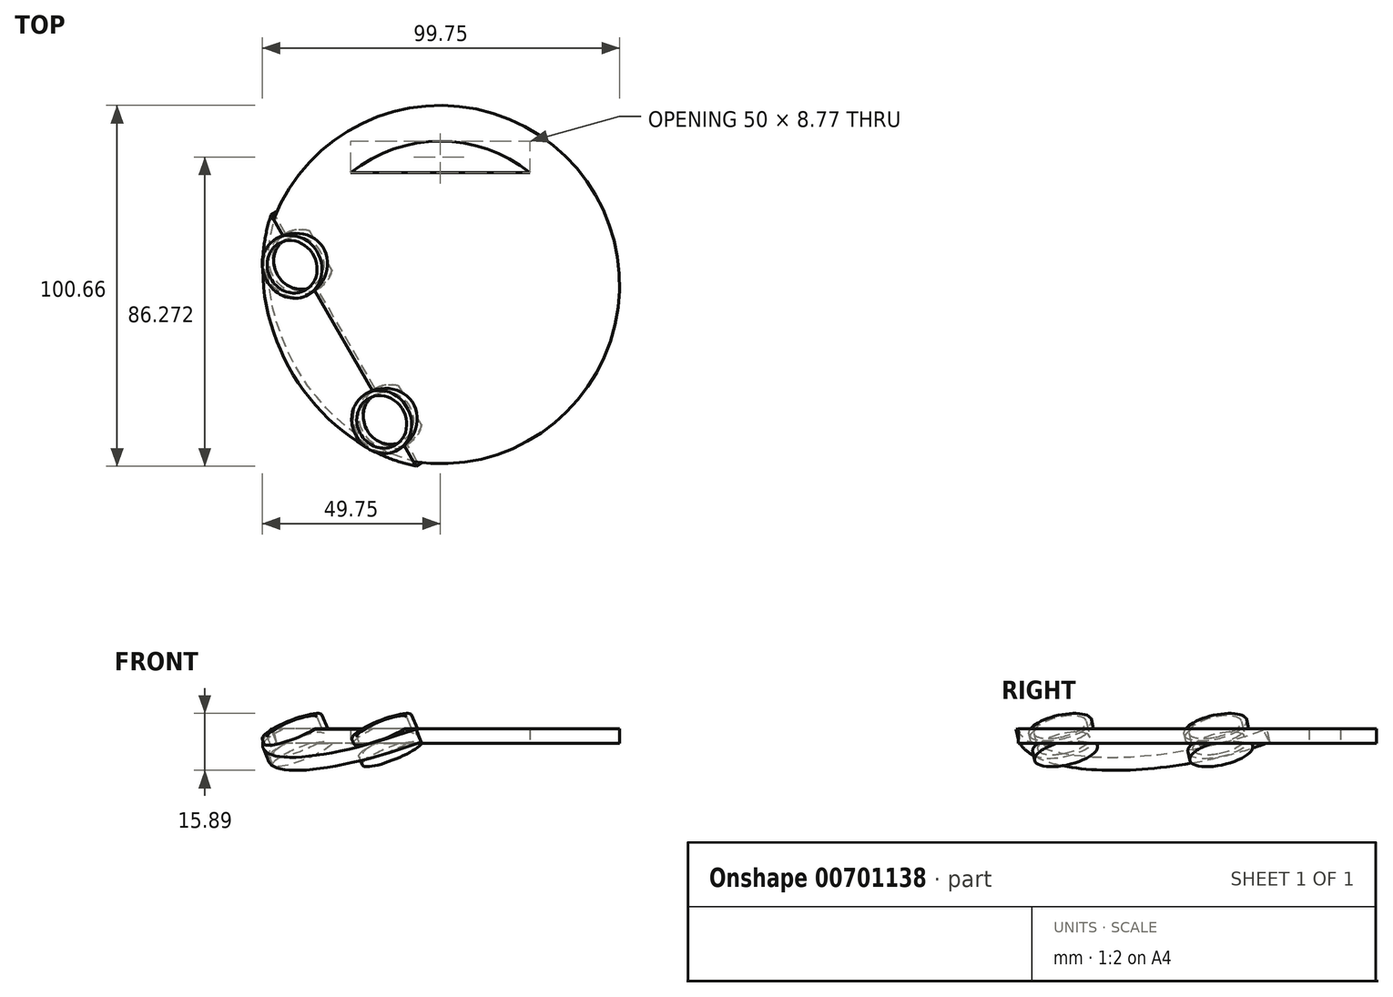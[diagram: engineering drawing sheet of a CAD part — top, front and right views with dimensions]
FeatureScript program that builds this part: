
annotation { "Feature Type Name" : "Feature", "Feature Type Description" : "" }
export const myFeature = defineFeature(function(context is Context, id is Id, definition is map)
    precondition{}
    {
        {
            var Q0;
            Q0=qCreatedBy(makeId("Top.planeOp"),FACE);
            var sketch = newSketch(context, id + "F0", { "sketchPlane" : qUnion([Q0])});
            skCircle(sketch, "E0", {"center": v(0, 0) * mm, "radius": 40 * mm});
            skLineSegment(sketch, "E1", {"start": v(-25, 31.22) * mm, "end": v(25, 31.22) * mm});
            skLineSegment(sketch, "E2", {"start": v(39.54, 6.04) * mm, "end": v(14.54, -37.26) * mm});
            skLineSegment(sketch, "E3", {"start": v(-39.54, 6.04) * mm, "end": v(-14.54, -37.26) * mm});
            skLineSegment(sketch, "E4", {"start": v(0, 0) * mm, "end": v(-27.04, -15.61) * mm});
            skLineSegment(sketch, "E5", {"start": v(0, 0) * mm, "end": v(0, 31.22) * mm});
            skLineSegment(sketch, "E6", {"start": v(0, 0) * mm, "end": v(27.04, -15.61) * mm});
            skCircle(sketch, "E7", {"center": v(0, 0) * mm, "radius": 50 * mm});
            skLineSegment(sketch, "E8", {"start": v(-39.54, 6.04) * mm, "end": v(-46.57, 18.2) * mm});
            skLineSegment(sketch, "E9", {"start": v(-14.54, -37.26) * mm, "end": v(-7.52, -49.43) * mm});
            skSolve(sketch);
        }
        {
            var Q0;
            Q0=sQuery(id+"F0.wireOp",EDGE,"E3");
            cPlane(context, id + "F1", {"entities" : qUnion([Q0]), "cplaneType" : CPlaneType.LINE_ANGLE, "offset" : 25 * mm, "angle" : 25 * degree, "width" : 150 * mm, "height" : 150 * mm});
        }
        {
            var Q0;
            {var subQ0=sQuery(id+"F0.wireOp",EDGE,"E5");Q0=makeQuery(id+"F0.imprint","IMPRINT",FACE,{"disambiguationData":[TD([[makeQuery(id+"F0.imprint","IMPRINT",EDGE,{"derivedFrom":subQ0}),-1.0]])]});}
            var Q1;
            {var subQ0=sQuery(id+"F0.wireOp",EDGE,"E4");Q1=makeQuery(id+"F0.imprint","IMPRINT",FACE,{"disambiguationData":[TD([[makeQuery(id+"F0.imprint","IMPRINT",EDGE,{"derivedFrom":subQ0}),1.0]])]});}
            var Q2;
            {var subQ3=sQuery(id+"F0.wireOp",EDGE,"E4");Q2=makeQuery(id+"F0.imprint","IMPRINT",FACE,{"disambiguationData":[TD([[makeQuery(id+"F0.imprint","IMPRINT",EDGE,{"derivedFrom":subQ3}),-1.0]])]});}
            var Q3;
            {var subQ0=sQuery(id+"F0.wireOp",EDGE,"E2");var subQ1=sQuery(id+"F0.wireOp",EDGE,"E0");var subQ2=makeQuery(id+"F0.imprint","INTERSECT",VERTEX,{"disambiguationData":[OD(0.0)],"derivedFrom":[subQ1,subQ0]});Q3=makeQuery(id+"F0.imprint","IMPRINT",FACE,{"disambiguationData":[TD([[makeQuery(id+"F0.imprint","IMPRINT",EDGE,{"disambiguationData":[TD([[subQ2,1.0]])],"derivedFrom":subQ1}),1.0]])]});}
            var Q4;
            {var subQ0=sQuery(id+"F0.wireOp",EDGE,"E1");var subQ1=sQuery(id+"F0.wireOp",EDGE,"E0");var subQ2=makeQuery(id+"F0.imprint","INTERSECT",VERTEX,{"disambiguationData":[OD(0.0)],"derivedFrom":[subQ1,subQ0]});Q4=makeQuery(id+"F0.imprint","IMPRINT",FACE,{"disambiguationData":[TD([[makeQuery(id+"F0.imprint","IMPRINT",EDGE,{"disambiguationData":[TD([[subQ2,1.0]])],"derivedFrom":subQ1}),1.0]])]});}
            var Q5;
            {var subQ7=sQuery(id+"F0.wireOp",EDGE,"E8");Q5=makeQuery(id+"F0.imprint","IMPRINT",FACE,{"disambiguationData":[TD([[makeQuery(id+"F0.imprint","IMPRINT",EDGE,{"derivedFrom":subQ7}),-1.0]])]});}
            extrude(context, id + "F2", {"entities" : qUnion([Q0, Q1, Q2, Q3, Q4, Q5]), "depth" : 4 * mm, "offsetDistance" : 25 * mm});
        }
        {
            var Q0;
            Q0=qCreatedBy(id+"F1.planeOp",FACE);
            var sketch = newSketch(context, id + "F3", { "sketchPlane" : qUnion([Q0])});
            skLineSegment(sketch, "E10.0", {"start": v(-37.3, -5.88) * mm, "end": v(-10.44, 36.29) * mm});
            skLineSegment(sketch, "E10.1", {"start": v(0, 0) * mm, "end": v(-23.87, 15.2) * mm, "construction": true});
            skCircle(sketch, "E11", {"center": v(-37.3, -5.88) * mm, "radius": 7.5 * mm});
            skCircle(sketch, "E12", {"center": v(-10.44, 36.29) * mm, "radius": 7.5 * mm});
            skCircle(sketch, "E13", {"center": v(-37.3, -5.88) * mm, "radius": 9 * mm});
            skCircle(sketch, "E14", {"center": v(-10.44, 36.29) * mm, "radius": 9 * mm});
            skLineSegment(sketch, "E15.0", {"start": v(-37.3, -5.88) * mm, "end": v(-44.85, -17.73) * mm});
            skLineSegment(sketch, "E15.1", {"start": v(-10.44, 36.29) * mm, "end": v(-2.89, 48.14) * mm});
            skEllipse(sketch, "E16.0", {"center": v(0, 0) * mm, "majorRadius": 50 * mm, "minorRadius": 45.32 * mm, "majorAxis": v(-0.54, -0.84)});
            skSolve(sketch);
        }
        {
            var Q0;
            Q0=makeQuery(id+"F3.imprint","IMPRINT",FACE,{"disambiguationData":[TD([[makeQuery(id+"F3.imprint","IMPRINT",EDGE,{"derivedFrom":sQuery(id+"F3.wireOp",EDGE,"E11")}),-1.0]])]});
            var Q1;
            Q1=makeQuery(id+"F3.imprint","IMPRINT",FACE,{"disambiguationData":[TD([[makeQuery(id+"F3.imprint","IMPRINT",EDGE,{"derivedFrom":sQuery(id+"F3.wireOp",EDGE,"E12")}),-1.0]])]});
            extrude(context, id + "F4", {"entities" : qUnion([Q0, Q1]), "operationType" : NewBodyOperationType.ADD, "oppositeDirection" : true, "depth" : 5 * mm, "offsetDistance" : 25 * mm});
        }
        {
            var Q0;
            Q0=makeQuery(id+"F3.imprint","IMPRINT",FACE,{"disambiguationData":[TD([[makeQuery(id+"F3.imprint","IMPRINT",EDGE,{"derivedFrom":sQuery(id+"F3.wireOp",EDGE,"E11")}),1.0]])]});
            var Q1;
            Q1=makeQuery(id+"F3.imprint","IMPRINT",FACE,{"disambiguationData":[TD([[makeQuery(id+"F3.imprint","IMPRINT",EDGE,{"derivedFrom":sQuery(id+"F3.wireOp",EDGE,"E12")}),1.0]])]});
            extrude(context, id + "F5", {"entities" : qUnion([Q0, Q1]), "operationType" : NewBodyOperationType.REMOVE, "endBound" : BoundingType.THROUGH_ALL, "depth" : 25 * mm, "offsetDistance" : 25 * mm, "hasSecondDirection" : true, "secondDirectionBound" : SecondDirectionBoundingType.THROUGH_ALL, "secondDirectionOppositeDirection" : true, "secondDirectionDepth" : 25 * mm});
        }
        {
            var Q0;
            Q0=makeQuery(id+"F3.imprint","IMPRINT",FACE,{"disambiguationData":[TD([[makeQuery(id+"F3.imprint","IMPRINT",EDGE,{"derivedFrom":sQuery(id+"F3.wireOp",EDGE,"E11")}),-1.0]])]});
            var Q1;
            Q1=makeQuery(id+"F3.imprint","IMPRINT",FACE,{"disambiguationData":[TD([[makeQuery(id+"F3.imprint","IMPRINT",EDGE,{"derivedFrom":sQuery(id+"F3.wireOp",EDGE,"E11")}),1.0]])]});
            var Q2;
            Q2=makeQuery(id+"F3.imprint","IMPRINT",FACE,{"disambiguationData":[TD([[makeQuery(id+"F3.imprint","IMPRINT",EDGE,{"derivedFrom":sQuery(id+"F3.wireOp",EDGE,"E12")}),-1.0]])]});
            var Q3;
            Q3=makeQuery(id+"F3.imprint","IMPRINT",FACE,{"disambiguationData":[TD([[makeQuery(id+"F3.imprint","IMPRINT",EDGE,{"derivedFrom":sQuery(id+"F3.wireOp",EDGE,"E12")}),1.0]])]});
            extrude(context, id + "F6", {"entities" : qUnion([Q0, Q1, Q2, Q3]), "operationType" : NewBodyOperationType.ADD, "depth" : 3 * mm, "offsetDistance" : 25 * mm});
        }
        {
            var Q0;
            Q0=qCreatedBy(id+"F1.planeOp",FACE);
            cPlane(context, id + "F7", {"entities" : qUnion([Q0]), "cplaneType" : CPlaneType.OFFSET, "offset" : 3.6 * mm, "oppositeDirection" : true, "width" : 150 * mm, "height" : 150 * mm});
        }
        {
            var Q0;
            Q0=qCreatedBy(id+"F7.planeOp",FACE);
            var sketch = newSketch(context, id + "F8", { "sketchPlane" : qUnion([Q0])});
            skLineSegment(sketch, "E17.0", {"start": v(-31.12, 0.67) * mm, "end": v(-13.76, 27.93) * mm});
            skLineSegment(sketch, "E17.1", {"start": v(-4.26, 42.84) * mm, "end": v(-1.46, 47.23) * mm});
            skCircle(sketch, "E17.2", {"center": v(-10.44, 36.29) * mm, "radius": 9 * mm});
            skEllipse(sketch, "E17.3", {"center": v(0, 0) * mm, "majorRadius": 50 * mm, "minorRadius": 45.32 * mm, "majorAxis": v(-0.54, -0.84)});
            skCircle(sketch, "E18.0", {"center": v(-37.3, -5.88) * mm, "radius": 9 * mm});
            skLineSegment(sketch, "E19", {"start": v(-1.46, 47.23) * mm, "end": v(-0.7, 48.43) * mm});
            skLineSegment(sketch, "E20", {"start": v(-31.12, 0.67) * mm, "end": v(-44.19, -19.84) * mm});
            skSolve(sketch);
        }
        {
            var Q0;
            {var subQ5=sQuery(id+"F8.wireOp",EDGE,"E17.0");Q0=makeQuery(id+"F8.imprint","IMPRINT",FACE,{"disambiguationData":[TD([[makeQuery(id+"F8.imprint","IMPRINT",EDGE,{"derivedFrom":subQ5}),1.0]])]});}
            extrude(context, id + "F9", {"entities" : qUnion([Q0]), "operationType" : NewBodyOperationType.ADD, "depth" : 4 * mm, "offsetDistance" : 25 * mm});
        }
    });
